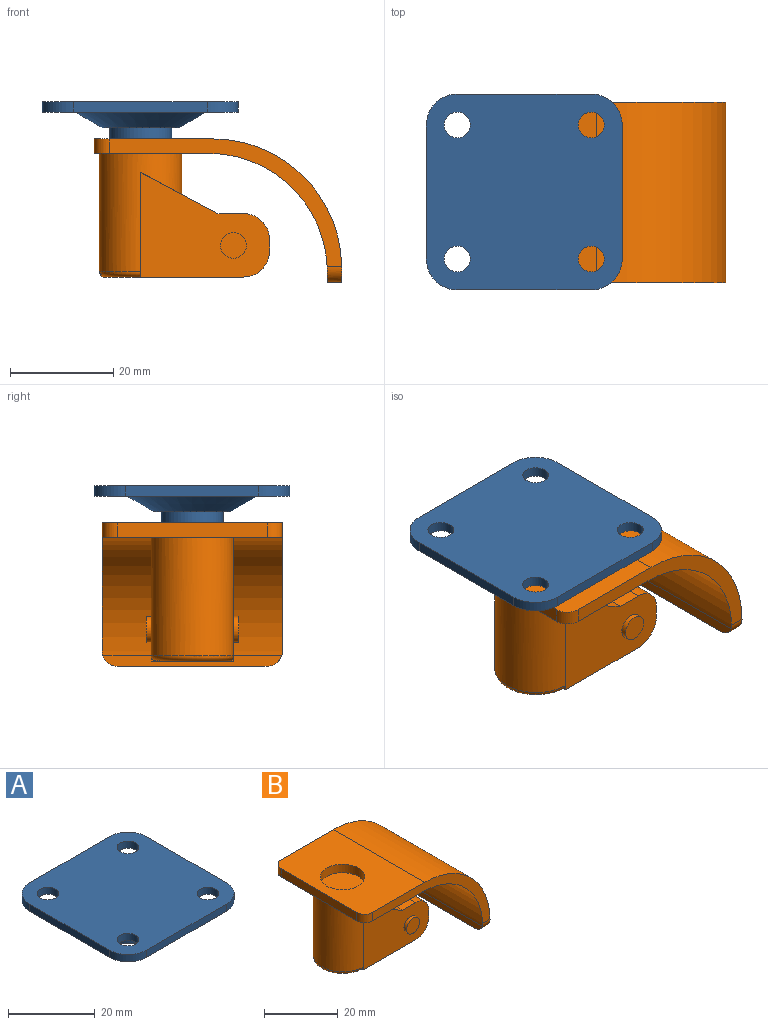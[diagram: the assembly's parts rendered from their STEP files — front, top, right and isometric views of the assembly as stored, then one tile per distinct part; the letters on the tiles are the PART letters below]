
ASSEMBLY  parts=2 mates=1
PART A: 19 faces, bbox 38x38x10 mm
  f0: plane 26x2mm, normal (0,1,0), area 52mm2, adj f1,f11,f12,f13
  f1: cylinder r=6mm len=6mm, axis (0,0,1), area 18.8mm2, adj f0,f2,f12,f13
  f2: plane 26x2mm, normal (-1,0,0), area 52mm2, adj f1,f3,f12,f13
  f3: cylinder r=6mm len=6mm, axis (0,0,1), area 18.8mm2, adj f2,f4,f12,f13
  f4: plane 26x2mm, normal (0,-1,0), area 52mm2, adj f3,f5,f12,f13
  f5: cylinder r=6mm len=6mm, axis (0,0,1), area 18.8mm2, adj f4,f6,f12,f13
  f6: plane 26x2mm, normal (1,0,0), area 52mm2, adj f5,f11,f12,f13
  f7: cylinder r=2.5mm len=5mm, axis (0,0,1), area 31.4mm2, adj f12,f13
  f8: cylinder r=2.5mm len=5mm, axis (0,0,1), area 31.4mm2, adj f12,f13
  f9: cylinder r=2.5mm len=5mm, axis (0,0,1), area 31.4mm2, adj f12,f13
  f10: cylinder r=2.5mm len=5mm, axis (0,0,1), area 31.4mm2, adj f12,f13
  f11: cylinder r=6mm len=6mm, axis (0,0,1), area 18.8mm2, adj f0,f6,f12,f13
  f12: plane 38x38mm, normal (0,0,-1), area 843.7mm2, adj f0,f1,f2,f3,f4,f5,f6,f7
  f13: plane 38x38mm, normal (0,0,1), area 1334.6mm2, adj f0,f1,f2,f3,f4,f5,f6,f7
  f14: cylinder r=12.5mm len=25mm, axis (0,0,1), area 8.9mm2, adj f12,f18
  f15: plane 15x15mm, normal (0,0,-1), area 63.6mm2, adj f16,f18
  f16: cylinder r=6mm len=12mm, axis (0,0,1), area 188.5mm2, adj f15,f17
  f17: plane 12x12mm, normal (0,0,-1), area 113.1mm2, adj f16
  f18: cone r=7.5mm half-angle=60deg, axis (0,0,1), area 362.8mm2, adj f14,f15
PART B: 33 faces, bbox 48.2x35.2x28 mm
  f0: plane 35x22.2mm, normal (0,0,-1), area 572.1mm2, adj f2,f3,f5,f9,f11,f12,f16
  f1: plane 34.99x2.8mm, normal (1,0,0), area 94.1mm2, adj f8,f10,f13,f14
  f2: plane 45x24.8mm, normal (0,-1,0), area 167mm2, adj f0,f6,f9,f10,f11,f13
  f3: plane 29x2.8mm, normal (-1,0,0), area 81.2mm2, adj f0,f6,f11,f12
  f4: cylinder r=6mm len=12mm, axis (0,0,1), area 105.6mm2, adj f6,f15
  f5: plane 45x24.8mm, normal (0,1,0), area 167mm2, adj f0,f6,f9,f10,f12,f14
  f6: plane 35x23mm, normal (0,0,1), area 688mm2, adj f2,f3,f4,f5,f10,f11,f12
  f7: plane 34.66x2mm, normal (-1,0,0), area 66.3mm2, adj f8,f9,f13,f14
  f8: plane 29x2.8mm, normal (0,0,-1), area 81.2mm2, adj f1,f7,f13,f14
  f9: cylinder r=23mm len=35mm, axis (0,-1,0), area 1264.3mm2, adj f0,f2,f5,f7,f13,f14
  f10: cylinder r=25mm len=35mm, axis (0,-1,0), area 1374.4mm2, adj f1,f2,f5,f6,f13,f14
  f11: cylinder r=3mm len=3mm, axis (0,0,1), area 13.2mm2, adj f0,f2,f3,f6
  f12: cylinder r=3mm len=3mm, axis (0,0,1), area 13.2mm2, adj f0,f3,f5,f6
  f13: cylinder r=3mm len=3mm, axis (-1,0,0), area 13.2mm2, adj f1,f2,f7,f8,f9,f10
  f14: cylinder r=3mm len=3mm, axis (-1,0,0), area 13.2mm2, adj f1,f5,f7,f8,f9,f10
  f15: plane 12x12mm, normal (0,0,1), area 113.1mm2, adj f4
  f16: cylinder r=8mm len=23mm, axis (0,0,1), area 753.5mm2, adj f0,f18,f20,f21,f24
  f17: plane 14x14mm, normal (0,0,-1), area 153.9mm2, adj f18,f19
  f18: torus R=7mm, axis (0,0,-1), area 37.8mm2, adj f16,f17,f20,f21,f23
  f19: plane 20x16mm, normal (0,0,-1), area 243mm2, adj f17,f20,f21,f22,f23,f28
  f20: plane 25.21x20.12mm, normal (0,1,0), area 322.8mm2, adj f16,f18,f19,f23,f24,f25,f26,f27
  f21: plane 20.31x1.04mm, normal (-1,0,0), area 0.9mm2, adj f16,f18,f19,f22,f24
  f22: plane 25x20.31mm, normal (0,-1,0), area 337.5mm2, adj f19,f21,f24,f25,f26,f27,f28,f29
  f23: plane 0.97x0.74mm, normal (-1,0,0), area 0.2mm2, adj f18,f19,f20
  f24: plane 16x15mm, normal (0.47,0,0.88), area 158.1mm2, adj f16,f20,f21,f22,f25
  f25: plane 16x5mm, normal (0,0,1), area 80mm2, adj f20,f22,f24,f27
  f26: plane 16x2.31mm, normal (1,0,0), area 37mm2, adj f20,f22,f27,f28
  f27: cylinder r=5mm len=16mm, axis (0,1,0), area 125.7mm2, adj f20,f22,f25,f26
  f28: cylinder r=5mm len=16mm, axis (0,-1,0), area 125.7mm2, adj f19,f20,f22,f26
  f29: cylinder r=2.5mm len=5mm, axis (0,1,0), area 15.7mm2, adj f22,f30
  f30: plane 5x5mm, normal (0,-1,0), area 19.6mm2, adj f29
  f31: cylinder r=2.5mm len=5mm, axis (0,-1,0), area 15.7mm2, adj f20,f32
  f32: plane 5x5mm, normal (0,1,0), area 19.6mm2, adj f31
PLACE A t=(-0.71,2.83,34)mm
PLACE B t=(-0.71,2.83,36.8)mm
MATE fastened A.f14 <-> B.f4  axis (0,0,-1) through (0,0,24)mm
